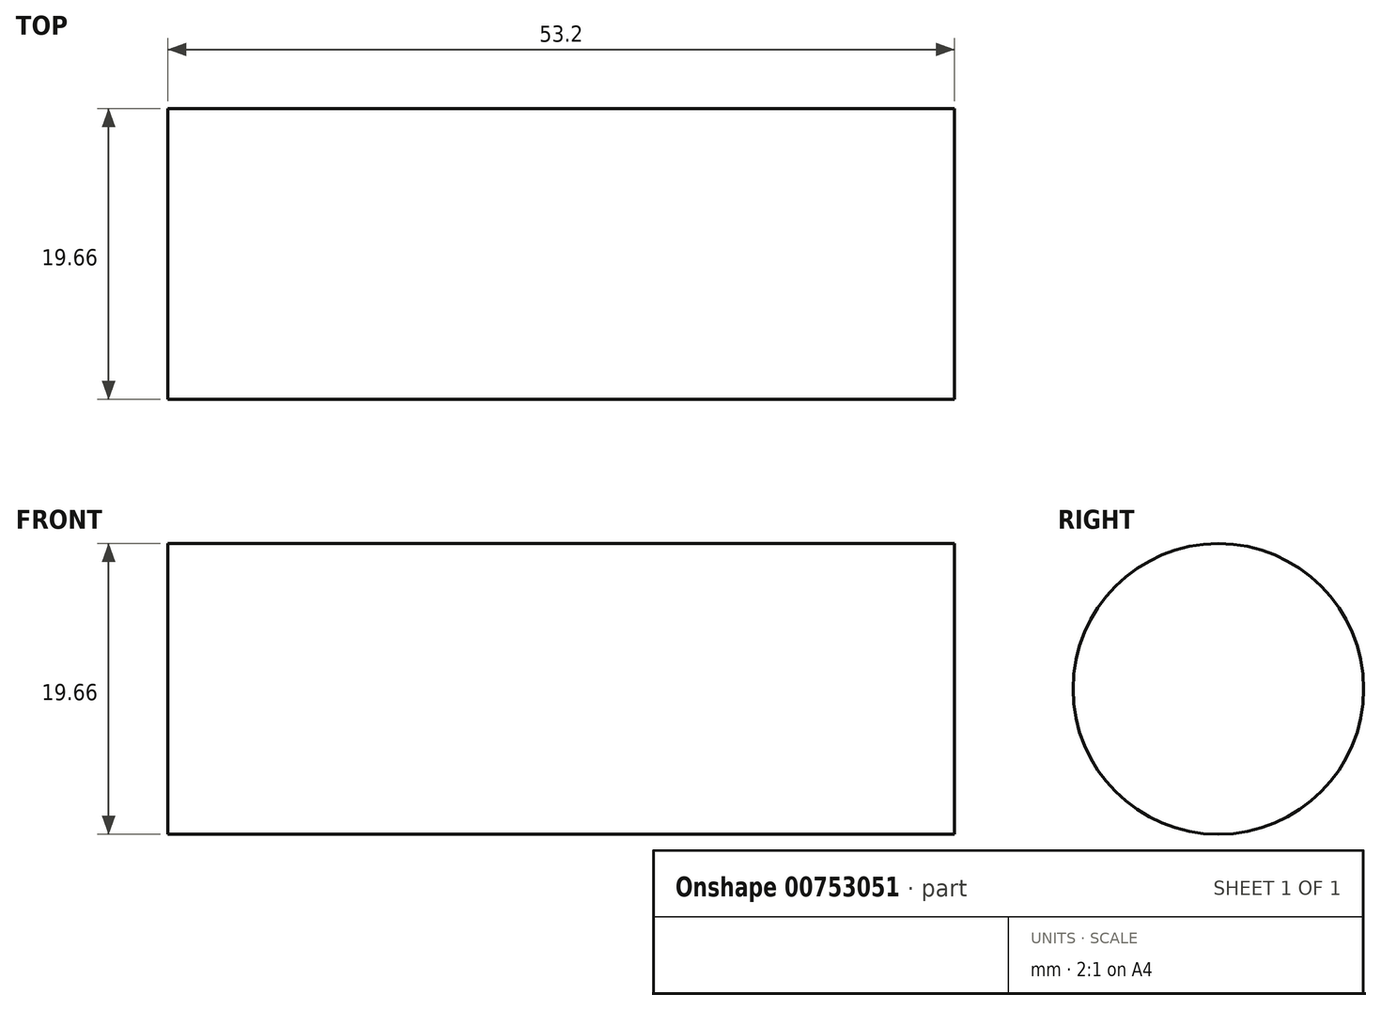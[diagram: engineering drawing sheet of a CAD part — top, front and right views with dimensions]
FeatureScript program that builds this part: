
annotation { "Feature Type Name" : "Feature", "Feature Type Description" : "" }
export const myFeature = defineFeature(function(context is Context, id is Id, definition is map)
    precondition{}
    {
        {
            var Q0;
            Q0=qCreatedBy(makeId("Front.planeOp"),FACE);
            var sketch = newSketch(context, id + "F0", { "sketchPlane" : qUnion([Q0])});
            skLineSegment(sketch, "E0", {"start": v(0, 0) * mm, "end": v(0, 9.83) * mm});
            skLineSegment(sketch, "E1", {"start": v(0, 9.83) * mm, "end": v(-53.2, 9.83) * mm});
            skLineSegment(sketch, "E2", {"start": v(-53.2, 9.83) * mm, "end": v(-53.2, 0) * mm});
            skLineSegment(sketch, "E3", {"start": v(-53.2, 0) * mm, "end": v(0, 0) * mm});
            skSolve(sketch);
        }
        {
            var Q0;
            Q0=sQuery(id+"F0.wireOp",EDGE,"E0");
            var Q1;
            Q1=sQuery(id+"F0.wireOp",EDGE,"E1");
            var Q2;
            Q2=sQuery(id+"F0.wireOp",EDGE,"E2");
            var Q3;
            Q3=sQuery(id+"F0.wireOp",EDGE,"E3");
            revolve(context, id + "F1", {"bodyType" : ToolBodyType.SURFACE, "surfaceOperationType" : NewSurfaceOperationType.NEW, "surfaceEntities" : qUnion([Q0, Q1, Q2]), "axis" : qUnion([Q3]), "revolveType" : RevolveType.FULL});
        }
    });
